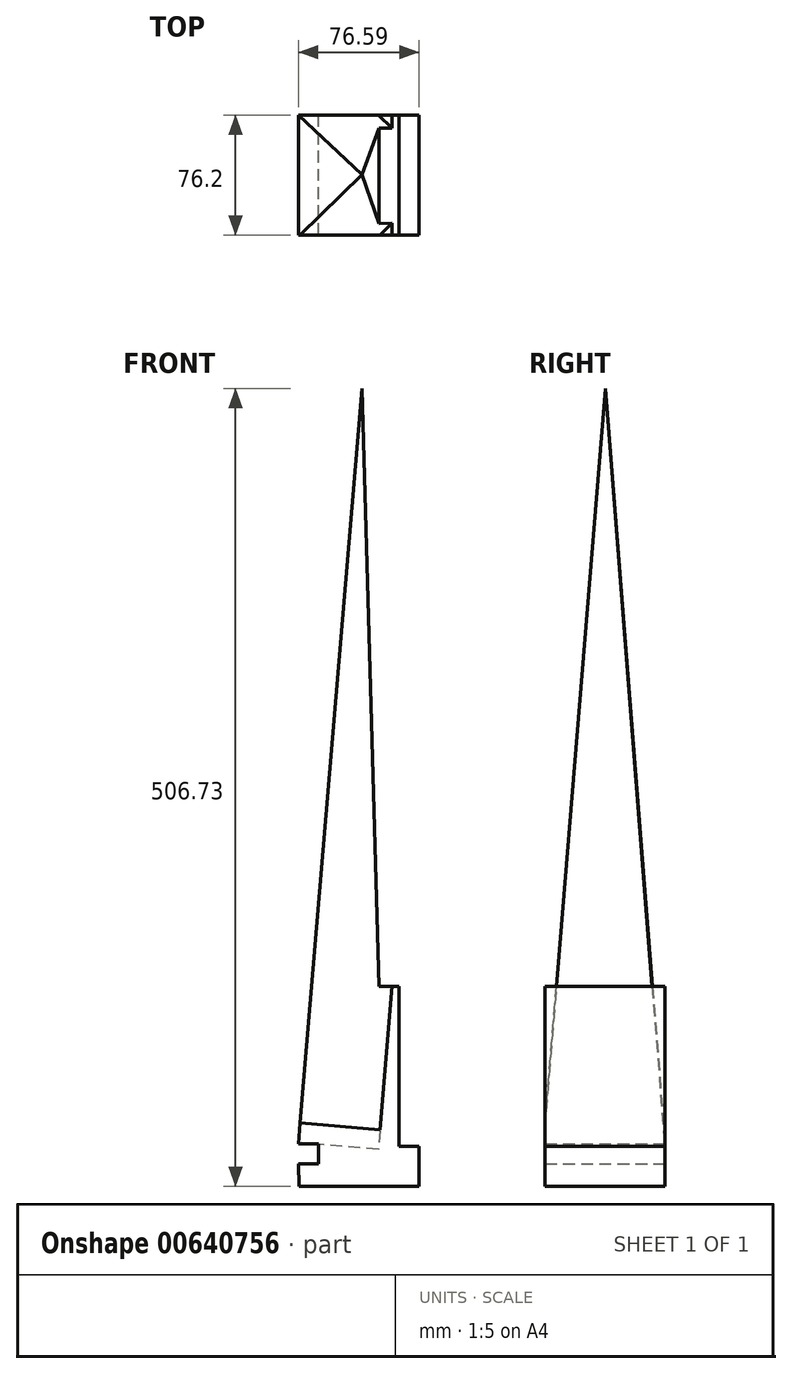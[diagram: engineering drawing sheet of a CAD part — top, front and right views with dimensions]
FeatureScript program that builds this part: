
annotation { "Feature Type Name" : "Feature", "Feature Type Description" : "" }
export const myFeature = defineFeature(function(context is Context, id is Id, definition is map)
    precondition{}
    {
        {
            var Q0;
            Q0=qCreatedBy(makeId("Front.planeOp"),FACE);
            var sketch = newSketch(context, id + "F0", { "sketchPlane" : qUnion([Q0])});
            skLineSegment(sketch, "E0", {"start": v(36.11, 1.72) * mm, "end": v(36.11, 27.12) * mm});
            skLineSegment(sketch, "E1", {"start": v(36.11, 27.12) * mm, "end": v(23.41, 27.12) * mm});
            skLineSegment(sketch, "E2", {"start": v(23.41, 27.12) * mm, "end": v(23.41, 128.72) * mm});
            skLineSegment(sketch, "E3", {"start": v(23.41, 128.72) * mm, "end": v(10.71, 128.72) * mm});
            skLineSegment(sketch, "E4", {"start": v(10.71, 128.72) * mm, "end": v(0, 509.57) * mm});
            skLineSegment(sketch, "E5", {"start": v(0, 509.57) * mm, "end": v(-40.48, 28.67) * mm});
            skPoint(sketch, "E6.endSnap0", {"position": v(-30.01, 1.72) * mm});
            skLineSegment(sketch, "E7", {"start": v(-40.09, 1.72) * mm, "end": v(36.11, 1.72) * mm});
            skLineSegment(sketch, "E8", {"start": v(-40.48, 28.67) * mm, "end": v(-27.78, 28.67) * mm});
            skLineSegment(sketch, "E9", {"start": v(-27.78, 28.67) * mm, "end": v(-27.78, 15.97) * mm});
            skLineSegment(sketch, "E10", {"start": v(-27.78, 15.97) * mm, "end": v(-40.48, 15.97) * mm});
            skLineSegment(sketch, "E11", {"start": v(-40.48, 15.97) * mm, "end": v(-40.09, 1.72) * mm});
            skSolve(sketch);
        }
        {
            var Q0;
            Q0=makeQuery(id+"F0.imprint","IMPRINT",FACE,{"disambiguationData":[TD([[makeQuery(id+"F0.imprint","IMPRINT",EDGE,{"derivedFrom":sQuery(id+"F0.wireOp",EDGE,"E0")}),1.0]])]});
            extrude(context, id + "F1", {"entities" : qUnion([Q0]), "depth" : 76.2 * mm, "offsetDistance" : 25.4 * mm});
        }
        {
            var Q0;
            Q0=makeQuery(id+"F1.opExtrude","SWEPT_FACE",FACE,{"disambiguationData":[OSD([sQuery(id+"F0.wireOp",EDGE,"E5")])]});
            var sketch = newSketch(context, id + "F2", { "sketchPlane" : qUnion([Q0])});
            skPoint(sketch, "E12", {"position": v(38.1, 507.77) * mm});
            skPoint(sketch, "E13", {"position": v(76.2, 25.17) * mm});
            skPoint(sketch, "E14", {"position": v(0, 25.17) * mm});
            skSolve(sketch);
        }
        {
            var Q0;
            {var subQ0=sQuery(id+"F0.wireOp",EDGE,"E5");Q0=makeQuery(id+"F2.imprint","IMPRINT",FACE,{"disambiguationData":[TD([[makeQuery(id+"F2.imprint","IMPRINT",EDGE,{"derivedFrom":makeQuery(id+"F1.opExtrude","CAP_EDGE",EDGE,{"disambiguationData":[OSD([subQ0])],"isStart":true})}),1.0]])]});}
            var sketch = newSketch(context, id + "F3", { "sketchPlane" : qUnion([Q0])});
            skPoint(sketch, "E15", {"position": v(37.64, 509.51) * mm});
            skLineSegment(sketch, "E16", {"start": v(77.2, 26.3) * mm, "end": v(37.64, 509.51) * mm});
            skSolve(sketch);
        }
        {
            var Q0;
            {var subQ0=sQuery(id+"F3.wireOp",EDGE,"E16");var subQ1=sQuery(id+"F0.wireOp",EDGE,"E5");var subQ2=makeQuery(id+"F2.imprint","IMPRINT",EDGE,{"derivedFrom":makeQuery(id+"F1.opExtrude","CAP_EDGE",EDGE,{"disambiguationData":[OSD([subQ1])],"isStart":false})});var subQ3=makeQuery(id+"F3.imprint","INTERSECT",VERTEX,{"derivedFrom":[subQ2,subQ0]});Q0=makeQuery(id+"F3.imprint","IMPRINT",FACE,{"disambiguationData":[TD([[makeQuery(id+"F3.imprint","IMPRINT",EDGE,{"disambiguationData":[TD([[subQ3,-1.0]])],"derivedFrom":subQ0}),-1.0]])]});}
            extrude(context, id + "F4", {"entities" : qUnion([Q0]), "operationType" : NewBodyOperationType.REMOVE, "oppositeDirection" : true, "depth" : 25.4 * mm, "offsetDistance" : 25.4 * mm});
        }
        {
            var Q0;
            {var subQ0=sQuery(id+"F0.wireOp",EDGE,"E5");Q0=makeQuery(id+"F2.imprint","IMPRINT",FACE,{"disambiguationData":[TD([[makeQuery(id+"F2.imprint","IMPRINT",EDGE,{"derivedFrom":makeQuery(id+"F1.opExtrude","CAP_EDGE",EDGE,{"disambiguationData":[OSD([subQ0])],"isStart":true})}),1.0]])]});}
            var sketch = newSketch(context, id + "F5", { "sketchPlane" : qUnion([Q0])});
            skPoint(sketch, "E17", {"position": v(38.15, 510.1) * mm});
            skLineSegment(sketch, "E18", {"start": v(38.15, 510.1) * mm, "end": v(0, 25.97) * mm});
            skSolve(sketch);
        }
        {
            var Q0;
            {var subQ0=sQuery(id+"F5.wireOp",EDGE,"E18");var subQ1=sQuery(id+"F0.wireOp",EDGE,"E5");var subQ2=makeQuery(id+"F2.imprint","IMPRINT",EDGE,{"derivedFrom":makeQuery(id+"F1.opExtrude","CAP_EDGE",EDGE,{"disambiguationData":[OSD([subQ1])],"isStart":true})});var subQ3=makeQuery(id+"F5.imprint","INTERSECT",VERTEX,{"derivedFrom":[subQ2,subQ0]});Q0=makeQuery(id+"F5.imprint","IMPRINT",FACE,{"disambiguationData":[TD([[makeQuery(id+"F5.imprint","IMPRINT",EDGE,{"disambiguationData":[TD([[subQ3,1.0]])],"derivedFrom":subQ0}),-1.0]])]});}
            extrude(context, id + "F6", {"entities" : qUnion([Q0]), "operationType" : NewBodyOperationType.REMOVE, "oppositeDirection" : true, "depth" : 25.4 * mm, "offsetDistance" : 25.4 * mm});
        }
        {
            var Q0;
            Q0=makeQuery(id+"F4.boolean.opBoolean","COPY",FACE,{"derivedFrom":makeQuery(id+"F4.opExtrude","CAP_FACE",FACE,{"disambiguationData":[OSD([sQuery(id+"F0.wireOp",EDGE,"E4"),sQuery(id+"F0.wireOp",EDGE,"E5"),sQuery(id+"F3.wireOp",EDGE,"E16")])],"isStart":false})});
            extrude(context, id + "F7", {"entities" : qUnion([Q0]), "operationType" : NewBodyOperationType.REMOVE, "oppositeDirection" : true, "depth" : 25.4 * mm, "offsetDistance" : 25.4 * mm});
        }
        {
            var Q0;
            Q0=makeQuery(id+"F6.boolean.opBoolean","COPY",FACE,{"derivedFrom":makeQuery(id+"F6.opExtrude","CAP_FACE",FACE,{"disambiguationData":[OSD([sQuery(id+"F0.wireOp",EDGE,"E4"),sQuery(id+"F0.wireOp",EDGE,"E5"),sQuery(id+"F5.wireOp",EDGE,"E18")])],"isStart":false})});
            extrude(context, id + "F8", {"entities" : qUnion([Q0]), "operationType" : NewBodyOperationType.REMOVE, "oppositeDirection" : true, "depth" : 25.4 * mm, "offsetDistance" : 25.4 * mm});
        }
    });
